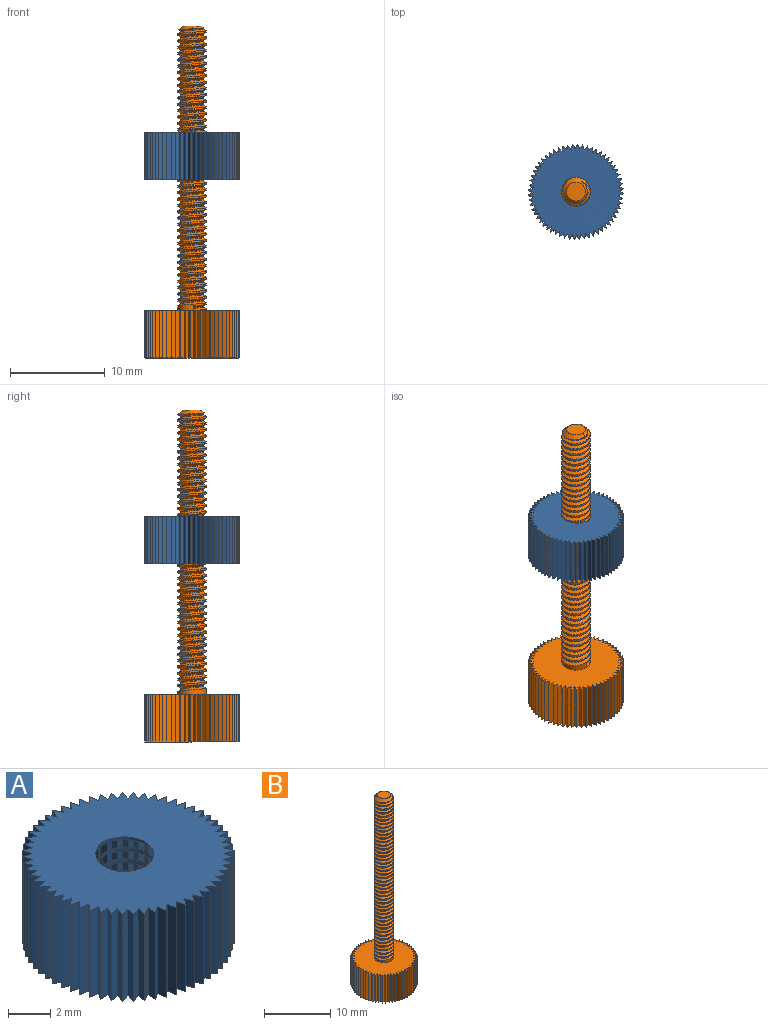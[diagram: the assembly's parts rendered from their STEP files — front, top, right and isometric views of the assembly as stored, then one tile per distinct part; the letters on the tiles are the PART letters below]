
ASSEMBLY  parts=2 mates=1
PART A: 124 faces, bbox 10x10x5 mm
  f0: plane 10.02x10.02mm, normal (0,0,-1), area 65mm2, adj f1,f2,f3,f4,f5,f6,f7,f8
  f1: plane 5x0.53mm, normal (0.06,1,0), area 2.7mm2, adj f0,f2,f120,f121
  f2: plane 5x0.44mm, normal (-0.83,-0.55,0), area 2.7mm2, adj f0,f1,f3,f121
  f3: plane 5x0.53mm, normal (-0.04,1,0), area 2.7mm2, adj f0,f2,f4,f121
  f4: plane 5x0.41mm, normal (-0.77,-0.64,0), area 2.7mm2, adj f0,f3,f5,f121
  f5: plane 5x0.52mm, normal (-0.15,0.99,0), area 2.7mm2, adj f0,f4,f6,f121
  f6: plane 5x0.38mm, normal (-0.7,-0.71,0), area 2.7mm2, adj f0,f5,f7,f121
  f7: plane 5x0.51mm, normal (-0.25,0.97,0), area 2.7mm2, adj f0,f6,f8,f121
  f8: plane 5x0.41mm, normal (-0.62,-0.78,0), area 2.7mm2, adj f0,f7,f9,f121
  f9: plane 5x0.5mm, normal (-0.35,0.94,0), area 2.7mm2, adj f0,f8,f10,f121
  f10: plane 5x0.45mm, normal (-0.54,-0.84,0), area 2.7mm2, adj f0,f9,f11,f121
  f11: plane 5x0.47mm, normal (-0.45,0.89,0), area 2.7mm2, adj f0,f10,f12,f121
  f12: plane 5x0.47mm, normal (-0.45,-0.89,0), area 2.7mm2, adj f0,f11,f13,f121
  f13: plane 5x0.45mm, normal (-0.54,0.84,0), area 2.7mm2, adj f0,f12,f14,f121
  f14: plane 5x0.5mm, normal (-0.35,-0.94,0), area 2.7mm2, adj f0,f13,f15,f121
  f15: plane 5x0.41mm, normal (-0.62,0.78,0), area 2.7mm2, adj f0,f14,f16,f121
  f16: plane 5x0.51mm, normal (-0.25,-0.97,0), area 2.7mm2, adj f0,f15,f17,f121
  f17: plane 5x0.38mm, normal (-0.7,0.71,0), area 2.7mm2, adj f0,f16,f18,f121
  f18: plane 5x0.52mm, normal (-0.15,-0.99,0), area 2.7mm2, adj f0,f17,f19,f121
  f19: plane 5x0.41mm, normal (-0.77,0.64,0), area 2.7mm2, adj f0,f18,f20,f121
  f20: plane 5x0.53mm, normal (-0.04,-1,0), area 2.7mm2, adj f0,f19,f21,f121
  f21: plane 5x0.44mm, normal (-0.83,0.55,0), area 2.7mm2, adj f0,f20,f22,f121
  f22: plane 5x0.53mm, normal (0.06,-1,0), area 2.7mm2, adj f0,f21,f23,f121
  f23: plane 5x0.47mm, normal (-0.89,0.46,0), area 2.7mm2, adj f0,f22,f24,f121
  f24: plane 5x0.52mm, normal (0.16,-0.99,0), area 2.7mm2, adj f0,f23,f25,f121
  f25: plane 5x0.49mm, normal (-0.93,0.37,0), area 2.7mm2, adj f0,f24,f26,f121
  f26: plane 5x0.51mm, normal (0.27,-0.96,0), area 2.7mm2, adj f0,f25,f27,f121
  f27: plane 5x0.51mm, normal (-0.96,0.27,0), area 2.7mm2, adj f0,f26,f28,f121
  f28: plane 5x0.49mm, normal (0.37,-0.93,0), area 2.7mm2, adj f0,f27,f29,f121
  f29: plane 5x0.52mm, normal (-0.99,0.16,0), area 2.7mm2, adj f0,f28,f30,f121
  f30: plane 5x0.47mm, normal (0.46,-0.89,0), area 2.7mm2, adj f0,f29,f31,f121
  f31: plane 5x0.53mm, normal (-1,0.06,0), area 2.7mm2, adj f0,f30,f32,f121
  f32: plane 5x0.44mm, normal (0.55,-0.83,0), area 2.7mm2, adj f0,f31,f33,f121
  f33: plane 5x0.53mm, normal (-1,-0.04,0), area 2.7mm2, adj f0,f32,f34,f121
  f34: plane 5x0.41mm, normal (0.64,-0.77,0), area 2.7mm2, adj f0,f33,f35,f121
  f35: plane 5x0.52mm, normal (-0.99,-0.15,0), area 2.7mm2, adj f0,f34,f36,f121
  f36: plane 5x0.38mm, normal (0.71,-0.7,0), area 2.7mm2, adj f0,f35,f37,f121
  f37: plane 5x0.51mm, normal (-0.97,-0.25,0), area 2.7mm2, adj f0,f36,f38,f121
  f38: plane 5x0.41mm, normal (0.78,-0.62,0), area 2.7mm2, adj f0,f37,f39,f121
  f39: plane 5x0.5mm, normal (-0.94,-0.35,0), area 2.7mm2, adj f0,f38,f40,f121
  f40: plane 5x0.45mm, normal (0.84,-0.54,0), area 2.7mm2, adj f0,f39,f41,f121
  f41: plane 5x0.47mm, normal (-0.89,-0.45,0), area 2.7mm2, adj f0,f40,f42,f121
  f42: plane 5x0.47mm, normal (0.89,-0.45,0), area 2.7mm2, adj f0,f41,f43,f121
  f43: plane 5x0.45mm, normal (-0.84,-0.54,0), area 2.7mm2, adj f0,f42,f44,f121
  f44: plane 5x0.5mm, normal (0.94,-0.35,0), area 2.7mm2, adj f0,f43,f45,f121
  f45: plane 5x0.41mm, normal (-0.78,-0.62,0), area 2.7mm2, adj f0,f44,f46,f121
  f46: plane 5x0.51mm, normal (0.97,-0.25,0), area 2.7mm2, adj f0,f45,f47,f121
  f47: plane 5x0.38mm, normal (-0.71,-0.7,0), area 2.7mm2, adj f0,f46,f48,f121
  f48: plane 5x0.52mm, normal (0.99,-0.15,0), area 2.7mm2, adj f0,f47,f49,f121
  f49: plane 5x0.41mm, normal (-0.64,-0.77,0), area 2.7mm2, adj f0,f48,f50,f121
  f50: plane 5x0.53mm, normal (1,-0.04,0), area 2.7mm2, adj f0,f49,f51,f121
  f51: plane 5x0.44mm, normal (-0.55,-0.83,0), area 2.7mm2, adj f0,f50,f52,f121
  f52: plane 5x0.53mm, normal (1,0.06,0), area 2.7mm2, adj f0,f51,f53,f121
  f53: plane 5x0.47mm, normal (-0.46,-0.89,0), area 2.7mm2, adj f0,f52,f54,f121
  f54: plane 5x0.52mm, normal (0.99,0.16,0), area 2.7mm2, adj f0,f53,f55,f121
  f55: plane 5x0.49mm, normal (-0.37,-0.93,0), area 2.7mm2, adj f0,f54,f56,f121
  f56: plane 5x0.51mm, normal (0.96,0.27,0), area 2.7mm2, adj f0,f55,f57,f121
  f57: plane 5x0.51mm, normal (-0.27,-0.96,0), area 2.7mm2, adj f0,f56,f58,f121
  f58: plane 5x0.49mm, normal (0.93,0.37,0), area 2.7mm2, adj f0,f57,f59,f121
  f59: plane 5x0.52mm, normal (-0.16,-0.99,0), area 2.7mm2, adj f0,f58,f60,f121
  f60: plane 5x0.47mm, normal (0.89,0.46,0), area 2.7mm2, adj f0,f59,f61,f121
  f61: plane 5x0.53mm, normal (-0.06,-1,0), area 2.7mm2, adj f0,f60,f62,f121
  f62: plane 5x0.44mm, normal (0.83,0.55,0), area 2.7mm2, adj f0,f61,f63,f121
  f63: plane 5x0.53mm, normal (0.04,-1,0), area 2.7mm2, adj f0,f62,f64,f121
  f64: plane 5x0.41mm, normal (0.77,0.64,0), area 2.7mm2, adj f0,f63,f65,f121
  f65: plane 5x0.52mm, normal (0.15,-0.99,0), area 2.7mm2, adj f0,f64,f66,f121
  f66: plane 5x0.38mm, normal (0.7,0.71,0), area 2.7mm2, adj f0,f65,f67,f121
  f67: plane 5x0.51mm, normal (0.25,-0.97,0), area 2.7mm2, adj f0,f66,f68,f121
  f68: plane 5x0.41mm, normal (0.62,0.78,0), area 2.7mm2, adj f0,f67,f69,f121
  f69: plane 5x0.5mm, normal (0.35,-0.94,0), area 2.7mm2, adj f0,f68,f70,f121
  f70: plane 5x0.45mm, normal (0.54,0.84,0), area 2.7mm2, adj f0,f69,f71,f121
  f71: plane 5x0.47mm, normal (0.45,-0.89,0), area 2.7mm2, adj f0,f70,f72,f121
  f72: plane 5x0.47mm, normal (0.45,0.89,0), area 2.7mm2, adj f0,f71,f73,f121
  f73: plane 5x0.45mm, normal (0.54,-0.84,0), area 2.7mm2, adj f0,f72,f74,f121
  f74: plane 5x0.5mm, normal (0.35,0.94,0), area 2.7mm2, adj f0,f73,f75,f121
  f75: plane 5x0.41mm, normal (0.62,-0.78,0), area 2.7mm2, adj f0,f74,f76,f121
  f76: plane 5x0.51mm, normal (0.25,0.97,0), area 2.7mm2, adj f0,f75,f77,f121
  f77: plane 5x0.38mm, normal (0.7,-0.71,0), area 2.7mm2, adj f0,f76,f78,f121
  f78: plane 5x0.52mm, normal (0.15,0.99,0), area 2.7mm2, adj f0,f77,f79,f121
  f79: plane 5x0.41mm, normal (0.77,-0.64,0), area 2.7mm2, adj f0,f78,f80,f121
  f80: plane 5x0.53mm, normal (0.04,1,0), area 2.7mm2, adj f0,f79,f81,f121
  f81: plane 5x0.44mm, normal (0.83,-0.55,0), area 2.7mm2, adj f0,f80,f82,f121
  f82: plane 5x0.53mm, normal (-0.06,1,0), area 2.7mm2, adj f0,f81,f83,f121
  f83: plane 5x0.47mm, normal (0.89,-0.46,0), area 2.7mm2, adj f0,f82,f84,f121
  f84: plane 5x0.52mm, normal (-0.16,0.99,0), area 2.7mm2, adj f0,f83,f85,f121
  f85: plane 5x0.49mm, normal (0.93,-0.37,0), area 2.7mm2, adj f0,f84,f86,f121
  f86: plane 5x0.51mm, normal (-0.27,0.96,0), area 2.7mm2, adj f0,f85,f87,f121
  f87: plane 5x0.51mm, normal (0.96,-0.27,0), area 2.7mm2, adj f0,f86,f88,f121
  f88: plane 5x0.49mm, normal (-0.37,0.93,0), area 2.7mm2, adj f0,f87,f89,f121
  f89: plane 5x0.52mm, normal (0.99,-0.16,0), area 2.7mm2, adj f0,f88,f90,f121
  f90: plane 5x0.47mm, normal (-0.46,0.89,0), area 2.7mm2, adj f0,f89,f91,f121
  f91: plane 5x0.53mm, normal (1,-0.06,0), area 2.7mm2, adj f0,f90,f92,f121
  f92: plane 5x0.44mm, normal (-0.55,0.83,0), area 2.7mm2, adj f0,f91,f93,f121
  f93: plane 5x0.53mm, normal (1,0.04,0), area 2.7mm2, adj f0,f92,f94,f121
  f94: plane 5x0.41mm, normal (-0.64,0.77,0), area 2.7mm2, adj f0,f93,f95,f121
  f95: plane 5x0.52mm, normal (0.99,0.15,0), area 2.7mm2, adj f0,f94,f96,f121
  f96: plane 5x0.38mm, normal (-0.71,0.7,0), area 2.7mm2, adj f0,f95,f97,f121
  f97: plane 5x0.51mm, normal (0.97,0.25,0), area 2.7mm2, adj f0,f96,f98,f121
  f98: plane 5x0.41mm, normal (-0.78,0.62,0), area 2.7mm2, adj f0,f97,f99,f121
  f99: plane 5x0.5mm, normal (0.94,0.35,0), area 2.7mm2, adj f0,f98,f100,f121
  f100: plane 5x0.45mm, normal (-0.84,0.54,0), area 2.7mm2, adj f0,f99,f101,f121
  f101: plane 5x0.47mm, normal (0.89,0.45,0), area 2.7mm2, adj f0,f100,f102,f121
  f102: plane 5x0.47mm, normal (-0.89,0.45,0), area 2.7mm2, adj f0,f101,f103,f121
  f103: plane 5x0.45mm, normal (0.84,0.54,0), area 2.7mm2, adj f0,f102,f104,f121
  f104: plane 5x0.5mm, normal (-0.94,0.35,0), area 2.7mm2, adj f0,f103,f105,f121
  f105: plane 5x0.41mm, normal (0.78,0.62,0), area 2.7mm2, adj f0,f104,f106,f121
  f106: plane 5x0.51mm, normal (-0.97,0.25,0), area 2.7mm2, adj f0,f105,f107,f121
  f107: plane 5x0.38mm, normal (0.71,0.7,0), area 2.7mm2, adj f0,f106,f108,f121
  f108: plane 5x0.52mm, normal (-0.99,0.15,0), area 2.7mm2, adj f0,f107,f109,f121
  f109: plane 5x0.41mm, normal (0.64,0.77,0), area 2.7mm2, adj f0,f108,f110,f121
  f110: plane 5x0.53mm, normal (-1,0.04,0), area 2.7mm2, adj f0,f109,f111,f121
  f111: plane 5x0.44mm, normal (0.55,0.83,0), area 2.7mm2, adj f0,f110,f112,f121
  f112: plane 5x0.53mm, normal (-1,-0.06,0), area 2.7mm2, adj f0,f111,f113,f121
  f113: plane 5x0.47mm, normal (0.46,0.89,0), area 2.7mm2, adj f0,f112,f114,f121
  f114: plane 5x0.52mm, normal (-0.99,-0.16,0), area 2.7mm2, adj f0,f113,f115,f121
  f115: plane 5x0.49mm, normal (0.37,0.93,0), area 2.7mm2, adj f0,f114,f116,f121
  f116: plane 5x0.51mm, normal (-0.96,-0.27,0), area 2.7mm2, adj f0,f115,f117,f121
  f117: plane 5x0.51mm, normal (0.27,0.96,0), area 2.7mm2, adj f0,f116,f118,f121
  f118: plane 5x0.49mm, normal (-0.93,-0.37,0), area 2.7mm2, adj f0,f117,f119,f121
  f119: plane 5x0.52mm, normal (0.16,0.99,0), area 2.7mm2, adj f0,f118,f120,f121
  f120: plane 5x0.47mm, normal (-0.89,-0.46,0), area 2.7mm2, adj f0,f1,f119,f121
  f121: plane 10.01x10.01mm, normal (0,0,1), area 65.1mm2, adj f1,f2,f3,f4,f5,f6,f7,f8
  f122: cylinder r=1.52mm len=5mm, axis (0,0,1), area 16.8mm2, adj f0,f121
  f123: cylinder r=1.22mm len=5mm, axis (0,0,-1), area 5mm2, adj f0,f121
PART B: 129 faces, bbox 10x10x35.1 mm
  f0: cylinder r=1.5mm len=29.5mm, axis (0,0,1), area 41.7mm2, adj f121,f124,f125,f126,f128
  f1: plane 5x0.53mm, normal (0.06,1,0), area 2.7mm2, adj f2,f120,f121,f122
  f2: plane 5x0.44mm, normal (-0.83,-0.55,0), area 2.7mm2, adj f1,f3,f121,f122
  f3: plane 5x0.53mm, normal (-0.04,1,0), area 2.7mm2, adj f2,f4,f121,f122
  f4: plane 5x0.41mm, normal (-0.77,-0.64,0), area 2.7mm2, adj f3,f5,f121,f122
  f5: plane 5x0.52mm, normal (-0.15,0.99,0), area 2.7mm2, adj f4,f6,f121,f122
  f6: plane 5x0.38mm, normal (-0.7,-0.71,0), area 2.7mm2, adj f5,f7,f121,f122
  f7: plane 5x0.51mm, normal (-0.25,0.97,0), area 2.7mm2, adj f6,f8,f121,f122
  f8: plane 5x0.41mm, normal (-0.62,-0.78,0), area 2.7mm2, adj f7,f9,f121,f122
  f9: plane 5x0.5mm, normal (-0.35,0.94,0), area 2.7mm2, adj f8,f10,f121,f122
  f10: plane 5x0.45mm, normal (-0.54,-0.84,0), area 2.7mm2, adj f9,f11,f121,f122
  f11: plane 5x0.47mm, normal (-0.45,0.89,0), area 2.7mm2, adj f10,f12,f121,f122
  f12: plane 5x0.47mm, normal (-0.45,-0.89,0), area 2.7mm2, adj f11,f13,f121,f122
  f13: plane 5x0.45mm, normal (-0.54,0.84,0), area 2.7mm2, adj f12,f14,f121,f122
  f14: plane 5x0.5mm, normal (-0.35,-0.94,0), area 2.7mm2, adj f13,f15,f121,f122
  f15: plane 5x0.41mm, normal (-0.62,0.78,0), area 2.7mm2, adj f14,f16,f121,f122
  f16: plane 5x0.51mm, normal (-0.25,-0.97,0), area 2.7mm2, adj f15,f17,f121,f122
  f17: plane 5x0.38mm, normal (-0.7,0.71,0), area 2.7mm2, adj f16,f18,f121,f122
  f18: plane 5x0.52mm, normal (-0.15,-0.99,0), area 2.7mm2, adj f17,f19,f121,f122
  f19: plane 5x0.41mm, normal (-0.77,0.64,0), area 2.7mm2, adj f18,f20,f121,f122
  f20: plane 5x0.53mm, normal (-0.04,-1,0), area 2.7mm2, adj f19,f21,f121,f122
  f21: plane 5x0.44mm, normal (-0.83,0.55,0), area 2.7mm2, adj f20,f22,f121,f122
  f22: plane 5x0.53mm, normal (0.06,-1,0), area 2.7mm2, adj f21,f23,f121,f122
  f23: plane 5x0.47mm, normal (-0.89,0.46,0), area 2.7mm2, adj f22,f24,f121,f122
  f24: plane 5x0.52mm, normal (0.16,-0.99,0), area 2.7mm2, adj f23,f25,f121,f122
  f25: plane 5x0.49mm, normal (-0.93,0.37,0), area 2.7mm2, adj f24,f26,f121,f122
  f26: plane 5x0.51mm, normal (0.27,-0.96,0), area 2.7mm2, adj f25,f27,f121,f122
  f27: plane 5x0.51mm, normal (-0.96,0.27,0), area 2.7mm2, adj f26,f28,f121,f122
  f28: plane 5x0.49mm, normal (0.37,-0.93,0), area 2.7mm2, adj f27,f29,f121,f122
  f29: plane 5x0.52mm, normal (-0.99,0.16,0), area 2.7mm2, adj f28,f30,f121,f122
  f30: plane 5x0.47mm, normal (0.46,-0.89,0), area 2.7mm2, adj f29,f31,f121,f122
  f31: plane 5x0.53mm, normal (-1,0.06,0), area 2.7mm2, adj f30,f32,f121,f122
  f32: plane 5x0.44mm, normal (0.55,-0.83,0), area 2.7mm2, adj f31,f33,f121,f122
  f33: plane 5x0.53mm, normal (-1,-0.04,0), area 2.7mm2, adj f32,f34,f121,f122
  f34: plane 5x0.41mm, normal (0.64,-0.77,0), area 2.7mm2, adj f33,f35,f121,f122
  f35: plane 5x0.52mm, normal (-0.99,-0.15,0), area 2.7mm2, adj f34,f36,f121,f122
  f36: plane 5x0.38mm, normal (0.71,-0.7,0), area 2.7mm2, adj f35,f37,f121,f122
  f37: plane 5x0.51mm, normal (-0.97,-0.25,0), area 2.7mm2, adj f36,f38,f121,f122
  f38: plane 5x0.41mm, normal (0.78,-0.62,0), area 2.7mm2, adj f37,f39,f121,f122
  f39: plane 5x0.5mm, normal (-0.94,-0.35,0), area 2.7mm2, adj f38,f40,f121,f122
  f40: plane 5x0.45mm, normal (0.84,-0.54,0), area 2.7mm2, adj f39,f41,f121,f122
  f41: plane 5x0.47mm, normal (-0.89,-0.45,0), area 2.7mm2, adj f40,f42,f121,f122
  f42: plane 5x0.47mm, normal (0.89,-0.45,0), area 2.7mm2, adj f41,f43,f121,f122
  f43: plane 5x0.45mm, normal (-0.84,-0.54,0), area 2.7mm2, adj f42,f44,f121,f122
  f44: plane 5x0.5mm, normal (0.94,-0.35,0), area 2.7mm2, adj f43,f45,f121,f122
  f45: plane 5x0.41mm, normal (-0.78,-0.62,0), area 2.7mm2, adj f44,f46,f121,f122
  f46: plane 5x0.51mm, normal (0.97,-0.25,0), area 2.7mm2, adj f45,f47,f121,f122
  f47: plane 5x0.38mm, normal (-0.71,-0.7,0), area 2.7mm2, adj f46,f48,f121,f122
  f48: plane 5x0.52mm, normal (0.99,-0.15,0), area 2.7mm2, adj f47,f49,f121,f122
  f49: plane 5x0.41mm, normal (-0.64,-0.77,0), area 2.7mm2, adj f48,f50,f121,f122
  f50: plane 5x0.53mm, normal (1,-0.04,0), area 2.7mm2, adj f49,f51,f121,f122
  f51: plane 5x0.44mm, normal (-0.55,-0.83,0), area 2.7mm2, adj f50,f52,f121,f122
  f52: plane 5x0.53mm, normal (1,0.06,0), area 2.7mm2, adj f51,f53,f121,f122
  f53: plane 5x0.47mm, normal (-0.46,-0.89,0), area 2.7mm2, adj f52,f54,f121,f122
  f54: plane 5x0.52mm, normal (0.99,0.16,0), area 2.7mm2, adj f53,f55,f121,f122
  f55: plane 5x0.49mm, normal (-0.37,-0.93,0), area 2.7mm2, adj f54,f56,f121,f122
  f56: plane 5x0.51mm, normal (0.96,0.27,0), area 2.7mm2, adj f55,f57,f121,f122
  f57: plane 5x0.51mm, normal (-0.27,-0.96,0), area 2.7mm2, adj f56,f58,f121,f122
  f58: plane 5x0.49mm, normal (0.93,0.37,0), area 2.7mm2, adj f57,f59,f121,f122
  f59: plane 5x0.52mm, normal (-0.16,-0.99,0), area 2.7mm2, adj f58,f60,f121,f122
  f60: plane 5x0.47mm, normal (0.89,0.46,0), area 2.7mm2, adj f59,f61,f121,f122
  f61: plane 5x0.53mm, normal (-0.06,-1,0), area 2.7mm2, adj f60,f62,f121,f122
  f62: plane 5x0.44mm, normal (0.83,0.55,0), area 2.7mm2, adj f61,f63,f121,f122
  f63: plane 5x0.53mm, normal (0.04,-1,0), area 2.7mm2, adj f62,f64,f121,f122
  f64: plane 5x0.41mm, normal (0.77,0.64,0), area 2.7mm2, adj f63,f65,f121,f122
  f65: plane 5x0.52mm, normal (0.15,-0.99,0), area 2.7mm2, adj f64,f66,f121,f122
  f66: plane 5x0.38mm, normal (0.7,0.71,0), area 2.7mm2, adj f65,f67,f121,f122
  f67: plane 5x0.51mm, normal (0.25,-0.97,0), area 2.7mm2, adj f66,f68,f121,f122
  f68: plane 5x0.41mm, normal (0.62,0.78,0), area 2.7mm2, adj f67,f69,f121,f122
  f69: plane 5x0.5mm, normal (0.35,-0.94,0), area 2.7mm2, adj f68,f70,f121,f122
  f70: plane 5x0.45mm, normal (0.54,0.84,0), area 2.7mm2, adj f69,f71,f121,f122
  f71: plane 5x0.47mm, normal (0.45,-0.89,0), area 2.7mm2, adj f70,f72,f121,f122
  f72: plane 5x0.47mm, normal (0.45,0.89,0), area 2.7mm2, adj f71,f73,f121,f122
  f73: plane 5x0.45mm, normal (0.54,-0.84,0), area 2.7mm2, adj f72,f74,f121,f122
  f74: plane 5x0.5mm, normal (0.35,0.94,0), area 2.7mm2, adj f73,f75,f121,f122
  f75: plane 5x0.41mm, normal (0.62,-0.78,0), area 2.7mm2, adj f74,f76,f121,f122
  f76: plane 5x0.51mm, normal (0.25,0.97,0), area 2.7mm2, adj f75,f77,f121,f122
  f77: plane 5x0.38mm, normal (0.7,-0.71,0), area 2.7mm2, adj f76,f78,f121,f122
  f78: plane 5x0.52mm, normal (0.15,0.99,0), area 2.7mm2, adj f77,f79,f121,f122
  f79: plane 5x0.41mm, normal (0.77,-0.64,0), area 2.7mm2, adj f78,f80,f121,f122
  f80: plane 5x0.53mm, normal (0.04,1,0), area 2.7mm2, adj f79,f81,f121,f122
  f81: plane 5x0.44mm, normal (0.83,-0.55,0), area 2.7mm2, adj f80,f82,f121,f122
  f82: plane 5x0.53mm, normal (-0.06,1,0), area 2.7mm2, adj f81,f83,f121,f122
  f83: plane 5x0.47mm, normal (0.89,-0.46,0), area 2.7mm2, adj f82,f84,f121,f122
  f84: plane 5x0.52mm, normal (-0.16,0.99,0), area 2.7mm2, adj f83,f85,f121,f122
  f85: plane 5x0.49mm, normal (0.93,-0.37,0), area 2.7mm2, adj f84,f86,f121,f122
  f86: plane 5x0.51mm, normal (-0.27,0.96,0), area 2.7mm2, adj f85,f87,f121,f122
  f87: plane 5x0.51mm, normal (0.96,-0.27,0), area 2.7mm2, adj f86,f88,f121,f122
  f88: plane 5x0.49mm, normal (-0.37,0.93,0), area 2.7mm2, adj f87,f89,f121,f122
  f89: plane 5x0.52mm, normal (0.99,-0.16,0), area 2.7mm2, adj f88,f90,f121,f122
  f90: plane 5x0.47mm, normal (-0.46,0.89,0), area 2.7mm2, adj f89,f91,f121,f122
  f91: plane 5x0.53mm, normal (1,-0.06,0), area 2.7mm2, adj f90,f92,f121,f122
  f92: plane 5x0.44mm, normal (-0.55,0.83,0), area 2.7mm2, adj f91,f93,f121,f122
  f93: plane 5x0.53mm, normal (1,0.04,0), area 2.7mm2, adj f92,f94,f121,f122
  f94: plane 5x0.41mm, normal (-0.64,0.77,0), area 2.7mm2, adj f93,f95,f121,f122
  f95: plane 5x0.52mm, normal (0.99,0.15,0), area 2.7mm2, adj f94,f96,f121,f122
  f96: plane 5x0.38mm, normal (-0.71,0.7,0), area 2.7mm2, adj f95,f97,f121,f122
  f97: plane 5x0.51mm, normal (0.97,0.25,0), area 2.7mm2, adj f96,f98,f121,f122
  f98: plane 5x0.41mm, normal (-0.78,0.62,0), area 2.7mm2, adj f97,f99,f121,f122
  f99: plane 5x0.5mm, normal (0.94,0.35,0), area 2.7mm2, adj f98,f100,f121,f122
  f100: plane 5x0.45mm, normal (-0.84,0.54,0), area 2.7mm2, adj f99,f101,f121,f122
  f101: plane 5x0.47mm, normal (0.89,0.45,0), area 2.7mm2, adj f100,f102,f121,f122
  f102: plane 5x0.47mm, normal (-0.89,0.45,0), area 2.7mm2, adj f101,f103,f121,f122
  f103: plane 5x0.45mm, normal (0.84,0.54,0), area 2.7mm2, adj f102,f104,f121,f122
  f104: plane 5x0.5mm, normal (-0.94,0.35,0), area 2.7mm2, adj f103,f105,f121,f122
  f105: plane 5x0.41mm, normal (0.78,0.62,0), area 2.7mm2, adj f104,f106,f121,f122
  f106: plane 5x0.51mm, normal (-0.97,0.25,0), area 2.7mm2, adj f105,f107,f121,f122
  f107: plane 5x0.38mm, normal (0.71,0.7,0), area 2.7mm2, adj f106,f108,f121,f122
  f108: plane 5x0.52mm, normal (-0.99,0.15,0), area 2.7mm2, adj f107,f109,f121,f122
  f109: plane 5x0.41mm, normal (0.64,0.77,0), area 2.7mm2, adj f108,f110,f121,f122
  f110: plane 5x0.53mm, normal (-1,0.04,0), area 2.7mm2, adj f109,f111,f121,f122
  f111: plane 5x0.44mm, normal (0.55,0.83,0), area 2.7mm2, adj f110,f112,f121,f122
  f112: plane 5x0.53mm, normal (-1,-0.06,0), area 2.7mm2, adj f111,f113,f121,f122
  f113: plane 5x0.47mm, normal (0.46,0.89,0), area 2.7mm2, adj f112,f114,f121,f122
  f114: plane 5x0.52mm, normal (-0.99,-0.16,0), area 2.7mm2, adj f113,f115,f121,f122
  f115: plane 5x0.49mm, normal (0.37,0.93,0), area 2.7mm2, adj f114,f116,f121,f122
  f116: plane 5x0.51mm, normal (-0.96,-0.27,0), area 2.7mm2, adj f115,f117,f121,f122
  f117: plane 5x0.51mm, normal (0.27,0.96,0), area 2.7mm2, adj f116,f118,f121,f122
  f118: plane 5x0.49mm, normal (-0.93,-0.37,0), area 2.7mm2, adj f117,f119,f121,f122
  f119: plane 5x0.52mm, normal (0.16,0.99,0), area 2.7mm2, adj f118,f120,f121,f122
  f120: plane 5x0.47mm, normal (-0.89,-0.46,0), area 2.7mm2, adj f1,f119,f121,f122
  f121: plane 10x10mm, normal (0,0,1), area 64.1mm2, adj f0,f1,f2,f3,f4,f5,f6,f7
  f122: plane 10x10mm, normal (0,0,-1), area 71.2mm2, adj f1,f2,f3,f4,f5,f6,f7,f8
  f123: plane 2x2mm, normal (0,0,1), area 3.1mm2, adj f124
  f124: cone r=1mm half-angle=45deg, axis (0,0,-1), area 3.8mm2, adj f0,f123,f126,f127,f128
  f125: plane 0.5x0.31mm, normal (0,1,0), area 0.1mm2, adj f0,f126,f127,f128
  f126: bspline ~29.75x3.46mm, area 133.1mm2, adj f0,f124,f125,f127
  f127: cylinder r=1.2mm len=29.61mm, axis (0,0,-1), area 41.5mm2, adj f124,f125,f126,f128
  f128: bspline ~29.86x3.46mm, area 132.8mm2, adj f0,f124,f125,f127
PLACE A rot(axis=(0,0,-1),146.2deg) t=(10.19,2.84,12.17)mm
PLACE B rot(axis=(0,0,-1),85.9deg) t=(1.39,-3.06,-6.64)mm fixed
MATE cylindrical B.f0 <-> A.f122  axis (0,0,1) through (1.39,-3.06,28.36)mm
